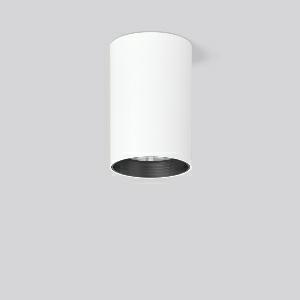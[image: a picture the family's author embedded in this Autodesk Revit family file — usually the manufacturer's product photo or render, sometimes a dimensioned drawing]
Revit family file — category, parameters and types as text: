
# Revit family: heledon_maxi_a_931235_002_283a
name_source: partatom
category: Lighting Fixtures
units: mm (PartAtom-declared; Revit-internal decimal feet)

## family parameters
Cut with Voids When Loaded = No
Host = Face
Light Source = No
Part Type = Normal
Room Calculation Point = No
Round Connector Dimension = Use Diameter
Shared = No

## types (1)
- HELEDON maxi A (1 x LED Modul 932 fresh meat, 1750 lm, 3200)
    Apparent Load = 33 VA
    Approval mark = CE
    CIE Flux Codes = 96 99 100 100 100
    Color Rendering = 90
    Color Temperature = 3200
    Default Elevation = 1800 mm
    Description = Series: HELEDON maxi
Cylindrical surface-mounted downlight. Housing: die-cast aluminium, powder-coated. Internal ceiling frame polycarbonate with bayonet mounting. Black plastic ring and recessed LED to prevent glare from the side. Optical assembly with lens made of plastic (polycarbonate) for the best homogeneous light distribution - can be changed without tools. Special LED for illumination of meat included. Suitable for Ceiling mounting. Easy installation with a separate ceiling frame with bayonet mounting and plug connection. Driver integrated. Connected via plug-in connector. High quality converter without flickering and stroboscopic effect. The following accessories can be mounted without use of tools: interchangeable lenses, decorative glasses, honeycomb louvre, clear and frosted diffusers, white interchangeable plastic ring. 
Colour: traffic white, matt (RAL 9016)
Diameter: 123 mm
Height: 183 mm
Lamp: LED
Socket: without socket
Colour temperature: fresh meat
System power: 33 W
Rated luminous flux: 1750 lm
Luminous efficiency: 53 lm/W
Control gear: Regulated power supply
Protection class: I
Type of protection: IP 20
    Height = 183 mm
    Lamp = 1 x LED Modul 932 fresh meat
    Lamp Light Flux = 1750 lm
    Lamp count = 1
    Length = 123 mm
    Lifetime = 50000 h
    Luminous efficacy = 53 lm/W
    Manufacturer = RZB
    ModVariant = No
    Model = 931235.002
    Mounting Place = Ceiling
    Mounting Type = Surface mounted
    Number of Poles = 1
    OnlyDefault = Yes
    Power Factor = 1
    Product Name = HELEDON maxi A
    Product group = Surface mounted downlights
    ProductGroupID = 302
    Protection Class = Protection class I
    Protection Degree = IP 20
    RLX_Detail_Level = 1
    RLX_Emergency_Light_Flux = 0 lm
    RLX_Emergency_Type = 0
    RLX_Emergency_Type_DB = No
    RlxData = <blob elided: 95797 chars, md5=b9fe8774>
    Socket = socket
    Standby Power = 0 W
    System Light Flux = 1750 lm
    System Power = 33 W
    Type Comments = Product without accessories
    Type Image = 931193.002.jpg
    URL = http://relux.com
    VarID = ---
    Voltage = 230 V
    Voltage Range = 220-240 V
    Weight = 0.00 kg
    Width = 0 mm  [stored 0 ft]

note: [stored X ft] marks values corroborated as IEEE doubles in the binary element streams (Revit-internal decimal feet)

## geometry (parser evidence)
native form markers: Blend x4, Sweep x11
no freeform markers — native parametric forms only
